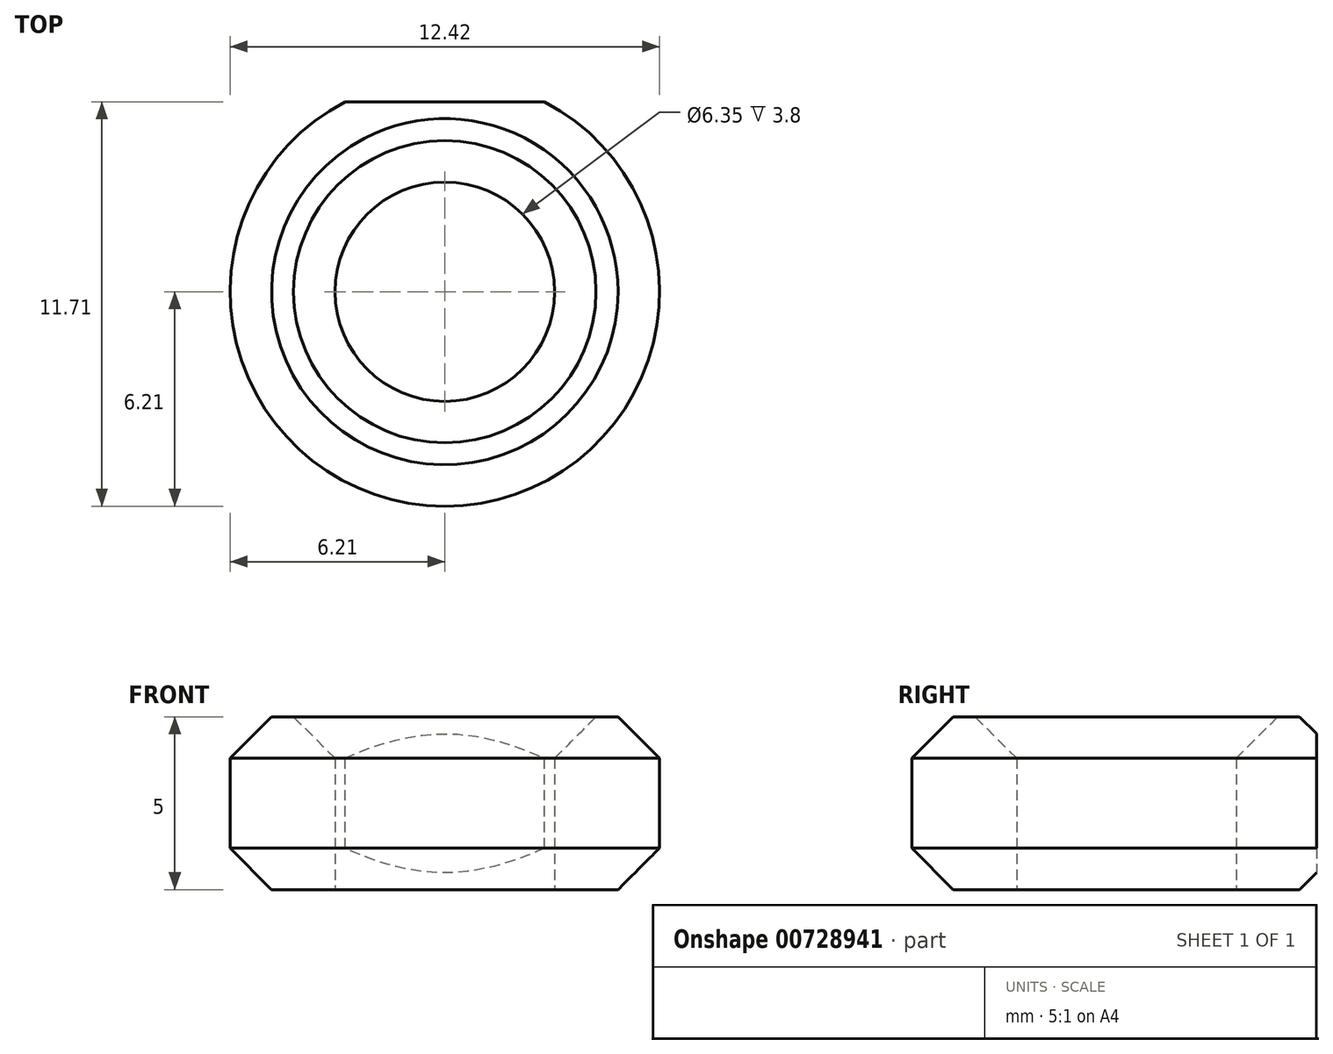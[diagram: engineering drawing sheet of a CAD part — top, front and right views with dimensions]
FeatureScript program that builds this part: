
annotation { "Feature Type Name" : "Feature", "Feature Type Description" : "" }
export const myFeature = defineFeature(function(context is Context, id is Id, definition is map)
    precondition{}
    {
        {
            var Q0;
            Q0=qCreatedBy(makeId("Top.planeOp"),FACE);
            var sketch = newSketch(context, id + "F0", { "sketchPlane" : qUnion([Q0])});
            skCircle(sketch, "E0", {"center": v(0, 0) * mm, "radius": 3.18 * mm});
            skCircle(sketch, "E1", {"center": v(0, 0) * mm, "radius": 6.21 * mm});
            skSolve(sketch);
        }
        {
            var Q0;
            Q0 = qSketchRegion(id + "F0", true);
            extrude(context, id + "F1", {"entities" : qUnion([Q0]), "depth" : 5 * mm, "offsetDistance" : 25 * mm});
        }
        {
            var Q0;
            Q0=makeQuery(id+"F1.opExtrude","CAP_EDGE",EDGE,{"disambiguationData":[OSD([sQuery(id+"F0.wireOp",EDGE,"E1")])],"isStart":false});
            var Q1;
            Q1=makeQuery(id+"F1.opExtrude","CAP_EDGE",EDGE,{"disambiguationData":[OSD([sQuery(id+"F0.wireOp",EDGE,"E1")])],"isStart":true});
            var Q2;
            Q2=makeQuery(id+"F1.opExtrude","CAP_EDGE",EDGE,{"disambiguationData":[OSD([sQuery(id+"F0.wireOp",EDGE,"E0")])],"isStart":false});
            chamfer(context, id + "F2", {"entities" : qUnion([Q0, Q1, Q2]), "width" : 1.2 * mm, "tangentPropagation" : true});
        }
        {
            var Q0;
            Q0=makeQuery(id+"F1.opExtrude","CAP_FACE",FACE,{"disambiguationData":[OSD([sQuery(id+"F0.wireOp",EDGE,"E0"),sQuery(id+"F0.wireOp",EDGE,"E1")])],"isStart":false});
            var sketch = newSketch(context, id + "F3", { "sketchPlane" : qUnion([Q0])});
            skCircle(sketch, "E2.0", {"center": v(0, 0) * mm, "radius": 6.21 * mm, "construction": true});
            skLineSegment(sketch, "E3.bottom", {"start": v(-2.89, 5.5) * mm, "end": v(2.89, 5.5) * mm});
            skLineSegment(sketch, "E3.top", {"start": v(-2.89, 6.21) * mm, "end": v(2.89, 6.21) * mm});
            skLineSegment(sketch, "E3.left", {"start": v(-2.89, 5.5) * mm, "end": v(-2.89, 6.21) * mm});
            skLineSegment(sketch, "E3.right", {"start": v(2.89, 5.5) * mm, "end": v(2.89, 6.21) * mm});
            skSolve(sketch);
        }
        {
            var Q0;
            Q0 = qSketchRegion(id + "F3", true);
            extrude(context, id + "F4", {"entities" : qUnion([Q0]), "operationType" : NewBodyOperationType.REMOVE, "endBound" : BoundingType.THROUGH_ALL, "oppositeDirection" : true, "depth" : 25 * mm, "offsetDistance" : 25 * mm});
        }
    });
